# Revit family: Rohrschelle Titan HD, ohne AG, o.D
name_source: partatom
category: HLS-Bauteile
revit_build: Autodesk Revit 2017 (Build: 20190507_1515(x64)
units: mm (PartAtom-declared; Revit-internal decimal feet)

## family parameters
Arbeitsebenenbasiert = Ja
Beim Laden mit Abzugskörper schneiden = Nein
Bemaßung runder Anschluss = Durchmesser verwenden
Gemeinsam genutzt = Ja
Immer vertikal = Nein
Raumberechnungspunkt = Nein
Teiletyp = Normal

## types (3) — shared parameters
Anschluss = ohne Anschluss
Bauart = zweiteilig
Brandschutz = RAL GZ 656
DF1 = 29 mm
DF2 = 14 mm  [stored 0.0459318 ft]
DVS = 13 mm
Fabrikat = MEFA
Firma = MEFA Befestigungs- und Montagesysteme GmbH
Kurztext1 = Rohrschelle Titan HD 50x5,0
MB = 50 mm  [stored 0.164042 ft]
MD = 5 mm  [stored 0.0164042 ft]
Material = Stahl
Materialmaße = 50x5,0 mm
Materialname = S235
Mengeneinheit = St
Oberflaeche = galvanisch verzinkt
Rohraußendurchmesser Zoll = Zoll
Verschluss = Schraubverschluss
Vorgabe-Ansicht = 1219 mm
max. zul. Last = 16.00 kN
max. zul. Last horizontal = 0.00 kN
max. zul. Last vertikal = 0.00 kN
vpe = 1 St
zero-valued in all types: Nennweite DN Rohr, Stärke Material, max. Rohraußendurchmesser, min. Rohraußendurchmesser

## per-type parameters (varying)
| type | Achsabstand | Artikelnummer | B | Breite | D | EAN | Gewicht | Gewicht pro Bauteil | H | Höhe | Kurztext2 | R | RM | Rohraußendurchmesser | S | max. Höhe |
| Titan HD, o.AG, Ø406, o.D. | 457 mm | 0070978 | 486 mm | 486 mm | 406 mm | 4250928403193 | 2.78 kg | 2.78 kg | 416 mm | 416 mm | 406 mm ohne Anschlussgewinde | 203 mm  [stored 0.66601 ft] | 208 mm | 406 mm | 457 mm  [stored 1.49934 ft] | 416 mm |
| Titan HD, o.AG, Ø457, o.D. | 508 mm | 00709887 | 537 mm  [stored 1.76181 ft] | 537 mm  [stored 1.76181 ft] | 457 mm  [stored 1.49934 ft] | 4250928403216 | 3.11 kg | 3.11 kg | 467 mm | 467 mm | 457 mm ohne Anschlussgewinde | 229 mm | 234 mm | 457 mm  [stored 1.49934 ft] | 508 mm  [stored 1.66667 ft] | 467 mm |
| Titan HD, o.AG, Ø508, o.D. | 559 mm | 0070995 | 588 mm  [stored 1.92913 ft] | 588 mm  [stored 1.92913 ft] | 508 mm  [stored 1.66667 ft] | 4250928403230 | 3.43 kg | 3.43 kg | 518 mm | 518 mm | 508 mm ohne Anschlussgewinde | 254 mm  [stored 0.833333 ft] | 259 mm | 508 mm  [stored 1.66667 ft] | 559 mm | 518 mm |

note: [stored X ft] marks values corroborated as IEEE doubles in the binary element streams (Revit-internal decimal feet)

## geometry (parser evidence)
native form markers: Sweep x6
no freeform markers — native parametric forms only
